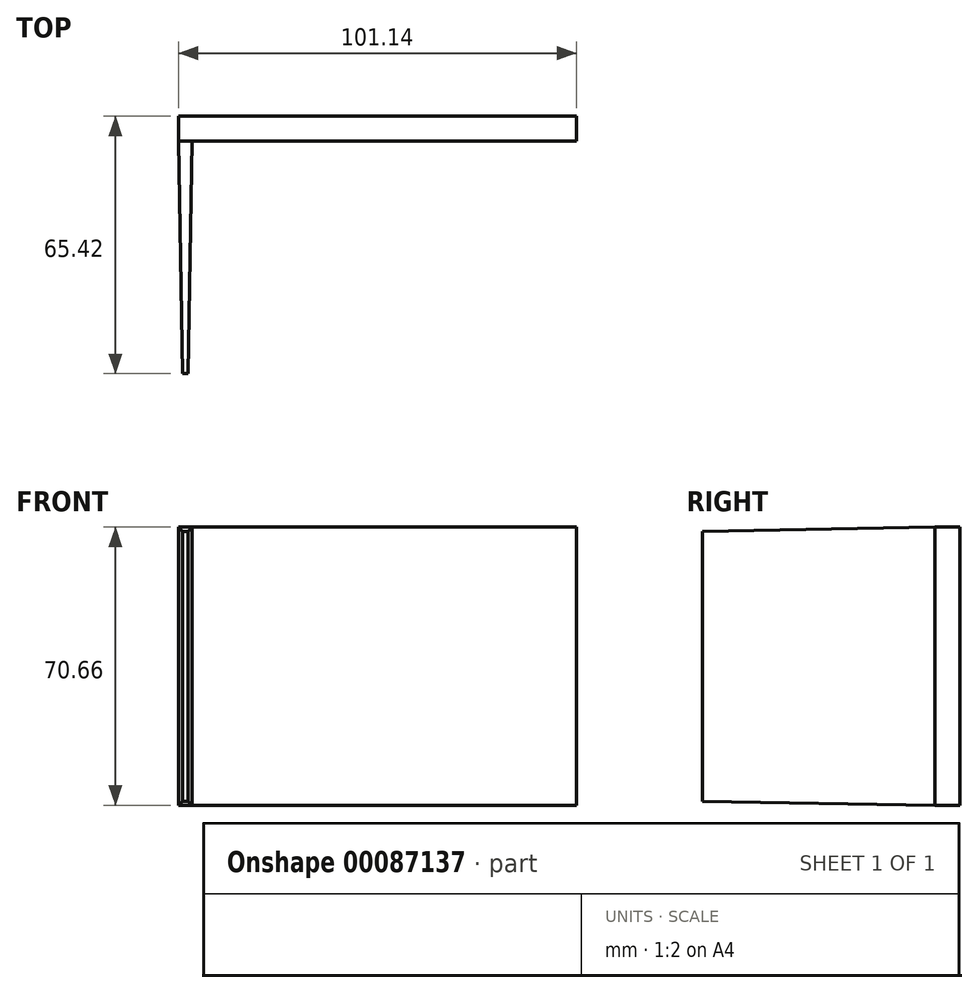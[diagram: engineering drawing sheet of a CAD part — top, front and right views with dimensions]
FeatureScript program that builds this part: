
annotation { "Feature Type Name" : "Feature", "Feature Type Description" : "" }
export const myFeature = defineFeature(function(context is Context, id is Id, definition is map)
    precondition{}
    {
        {
            var Q0;
            Q0=qCreatedBy(makeId("Front.planeOp"),FACE);
            var sketch = newSketch(context, id + "F0", { "sketchPlane" : qUnion([Q0])});
            skLineSegment(sketch, "E0.bottom", {"start": v(50.57, 35.33) * mm, "end": v(-50.57, 35.33) * mm});
            skLineSegment(sketch, "E0.top", {"start": v(50.57, -35.33) * mm, "end": v(-50.57, -35.33) * mm});
            skLineSegment(sketch, "E0.left", {"start": v(50.57, 35.33) * mm, "end": v(50.57, -35.33) * mm});
            skLineSegment(sketch, "E0.right", {"start": v(-50.57, 35.33) * mm, "end": v(-50.57, -35.33) * mm});
            skPoint(sketch, "E0.middle", {"position": v(0, 0) * mm});
            skSolve(sketch);
        }
        {
            var Q0;
            Q0 = qSketchRegion(id + "F0", true);
            extrude(context, id + "F1", {"entities" : qUnion([Q0]), "depth" : 6.35 * mm});
        }
        {
            var Q0;
            Q0=makeQuery(id+"F1.opExtrude","CAP_FACE",FACE,{"disambiguationData":[OSD([sQuery(id+"F0.wireOp",EDGE,"E0.bottom"),sQuery(id+"F0.wireOp",EDGE,"E0.top"),sQuery(id+"F0.wireOp",EDGE,"E0.left"),sQuery(id+"F0.wireOp",EDGE,"E0.right")])],"isStart":false});
            var sketch = newSketch(context, id + "F2", { "sketchPlane" : qUnion([Q0])});
            skLineSegment(sketch, "E1.bottom", {"start": v(-50.57, -35.33) * mm, "end": v(-47.12, -35.33) * mm});
            skLineSegment(sketch, "E1.top", {"start": v(-50.57, 35.33) * mm, "end": v(-47.12, 35.33) * mm});
            skLineSegment(sketch, "E1.left", {"start": v(-50.57, -35.33) * mm, "end": v(-50.57, 35.33) * mm});
            skLineSegment(sketch, "E1.right", {"start": v(-47.12, -35.33) * mm, "end": v(-47.12, 35.33) * mm});
            skSolve(sketch);
        }
        {
            var Q0;
            Q0 = qSketchRegion(id + "F2", true);
            extrude(context, id + "F3", {"entities" : qUnion([Q0]), "operationType" : NewBodyOperationType.ADD, "depth" : 59.07 * mm, "hasDraft" : true, "draftAngle" : 1 * degree, "draftPullDirection" : true});
        }
    });
